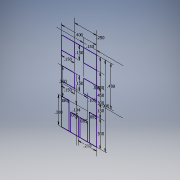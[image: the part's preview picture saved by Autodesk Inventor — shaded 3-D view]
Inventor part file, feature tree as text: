
AUTODESK INVENTOR PART (.ipt)
format: ipt  version: 2018 (Build 220112000, 112)  size: 115,200 bytes
history: native  units: in
note: dims shown in document units (in); Inventor stores cm internally (conversion verified against a paired STEP export)
features: sketch x1
ambient origin geometry x8: Origin, YZ Plane, XZ Plane, XY Plane, X Axis, Y Axis, Z Axis, Center Point
feature tree (1):
  sketch  "Sketch1"  dims[d16=0.4in d17=0.9in d18=0.3in d20=0.085in d21=0.085in d22=0.085in d23=0.085in d24=0.105in d25=0.21in d26=0.1035in d27=0.3in d28=0.15in d29=0.15in d30=0.15in d31=0.15in d33=0.45in d34=0.0in d35=0.25in d37=0.3in d38=0.15in d39=0.5998in d40=0.45in d41=0.3in d42=0.1498in]
